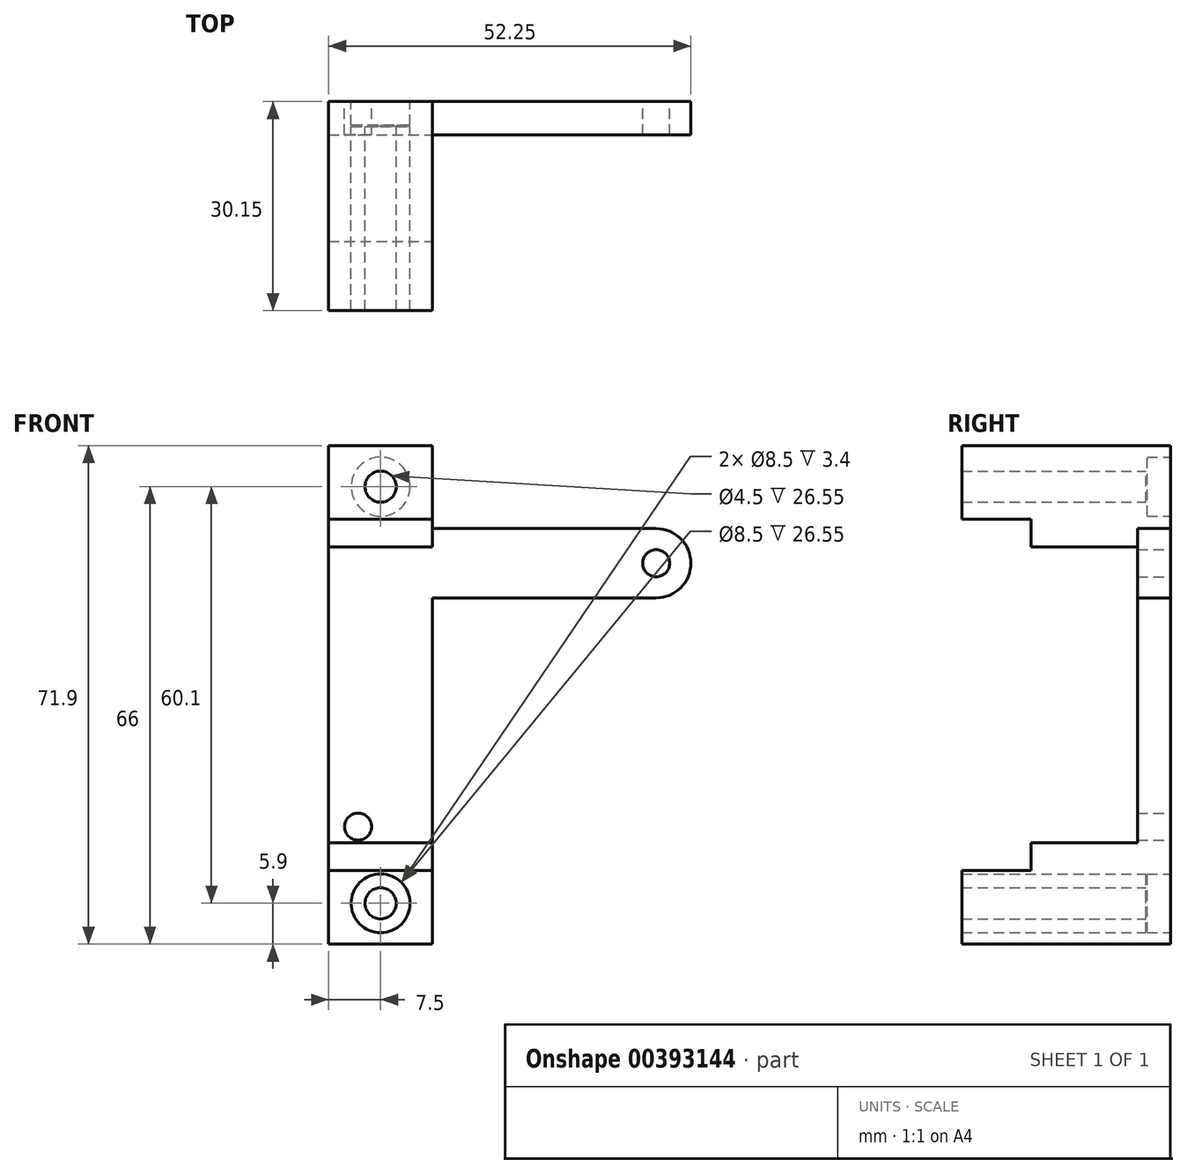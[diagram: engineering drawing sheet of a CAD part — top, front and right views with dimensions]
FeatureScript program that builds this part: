
annotation { "Feature Type Name" : "Feature", "Feature Type Description" : "" }
export const myFeature = defineFeature(function(context is Context, id is Id, definition is map)
    precondition{}
    {
        {
            var Q0;
            Q0=qCreatedBy(makeId("Front.planeOp"),FACE);
            var sketch = newSketch(context, id + "F0", { "sketchPlane" : qUnion([Q0])});
            skLineSegment(sketch, "E0", {"start": v(7.5, 35.95) * mm, "end": v(-7.5, 35.95) * mm});
            skPoint(sketch, "E1", {"position": v(0, 35.95) * mm});
            skLineSegment(sketch, "E2.MirrorCS", {"start": v(7.5, -35.95) * mm, "end": v(-7.5, -35.95) * mm});
            skPoint(sketch, "E3.MirrorP", {"position": v(0, -35.95) * mm});
            skLineSegment(sketch, "E4", {"start": v(-7.5, 35.95) * mm, "end": v(-7.5, -35.95) * mm});
            skLineSegment(sketch, "E5", {"start": v(7.5, -35.95) * mm, "end": v(7.5, 35.95) * mm});
            skLineSegment(sketch, "E6", {"start": v(-7.5, 25.35) * mm, "end": v(7.5, 25.35) * mm});
            skLineSegment(sketch, "E7", {"start": v(-7.5, 21.35) * mm, "end": v(7.5, 21.35) * mm});
            skLineSegment(sketch, "E8.MirrorCS", {"start": v(-7.5, -25.35) * mm, "end": v(7.5, -25.35) * mm});
            skLineSegment(sketch, "E9.MirrorCS", {"start": v(-7.5, -21.35) * mm, "end": v(7.5, -21.35) * mm});
            skCircle(sketch, "E10", {"center": v(0, 30.05) * mm, "radius": 2.25 * mm});
            skCircle(sketch, "E11", {"center": v(0, 30.05) * mm, "radius": 4.25 * mm});
            skCircle(sketch, "E12.MirrorC", {"center": v(0, -30.05) * mm, "radius": 2.25 * mm});
            skCircle(sketch, "E13.MirrorC", {"center": v(0, -30.05) * mm, "radius": 4.25 * mm});
            skCircle(sketch, "E14", {"center": v(39.75, 19) * mm, "radius": 1.95 * mm});
            skCircle(sketch, "E15", {"center": v(-3.25, -19) * mm, "radius": 1.95 * mm});
            skArc(sketch, "E16", {"start": v(39.75, 24) * mm, "mid": v(44.75, 19) * mm, "end": v(39.75, 14) * mm});
            skLineSegment(sketch, "E17", {"start": v(39.75, 24) * mm, "end": v(7.5, 24) * mm});
            skLineSegment(sketch, "E18", {"start": v(39.75, 14) * mm, "end": v(7.5, 14) * mm});
            skSolve(sketch);
        }
        {
            var Q0;
            {var subQ0=sQuery(id+"F0.wireOp",EDGE,"E7");Q0=makeQuery(id+"F0.imprint","IMPRINT",FACE,{"disambiguationData":[TD([[makeQuery(id+"F0.imprint","IMPRINT",EDGE,{"derivedFrom":subQ0}),-1.0]])]});}
            var Q1;
            Q1=makeQuery(id+"F0.imprint","IMPRINT",FACE,{"disambiguationData":[TD([[makeQuery(id+"F0.imprint","IMPRINT",EDGE,{"derivedFrom":sQuery(id+"F0.wireOp",EDGE,"E14")}),-1.0]])]});
            extrude(context, id + "F1", {"entities" : qUnion([Q0, Q1]), "depth" : 4.8 * mm});
        }
        {
            var Q0;
            {var subQ0=sQuery(id+"F0.wireOp",EDGE,"E6");Q0=makeQuery(id+"F0.imprint","IMPRINT",FACE,{"disambiguationData":[TD([[makeQuery(id+"F0.imprint","IMPRINT",EDGE,{"derivedFrom":subQ0}),-1.0]])]});}
            var Q1;
            {var subQ0=sQuery(id+"F0.wireOp",EDGE,"E8.MirrorCS");Q1=makeQuery(id+"F0.imprint","IMPRINT",FACE,{"disambiguationData":[TD([[makeQuery(id+"F0.imprint","IMPRINT",EDGE,{"derivedFrom":subQ0}),1.0]])]});}
            extrude(context, id + "F2", {"entities" : qUnion([Q0, Q1]), "operationType" : NewBodyOperationType.ADD, "depth" : (19.15 + 1) * mm});
        }
        {
            var Q0;
            {var subQ1=sQuery(id+"F0.wireOp",EDGE,"E0");Q0=makeQuery(id+"F0.imprint","IMPRINT",FACE,{"disambiguationData":[TD([[makeQuery(id+"F0.imprint","IMPRINT",EDGE,{"derivedFrom":subQ1}),1.0]])]});}
            var Q1;
            Q1=makeQuery(id+"F0.imprint","IMPRINT",FACE,{"disambiguationData":[TD([[makeQuery(id+"F0.imprint","IMPRINT",EDGE,{"derivedFrom":sQuery(id+"F0.wireOp",EDGE,"E10")}),-1.0]])]});
            var Q2;
            {var subQ2=sQuery(id+"F0.wireOp",EDGE,"E2.MirrorCS");Q2=makeQuery(id+"F0.imprint","IMPRINT",FACE,{"disambiguationData":[TD([[makeQuery(id+"F0.imprint","IMPRINT",EDGE,{"derivedFrom":subQ2}),-1.0]])]});}
            var Q3;
            Q3=makeQuery(id+"F0.imprint","IMPRINT",FACE,{"disambiguationData":[TD([[makeQuery(id+"F0.imprint","IMPRINT",EDGE,{"derivedFrom":sQuery(id+"F0.wireOp",EDGE,"E12.MirrorC")}),1.0]])]});
            extrude(context, id + "F3", {"entities" : qUnion([Q0, Q1, Q2, Q3]), "operationType" : NewBodyOperationType.ADD, "depth" : 30.15 * mm});
        }
        {
            var Q0;
            Q0=makeQuery(id+"F0.imprint","IMPRINT",FACE,{"disambiguationData":[TD([[makeQuery(id+"F0.imprint","IMPRINT",EDGE,{"derivedFrom":sQuery(id+"F0.wireOp",EDGE,"E12.MirrorC")}),1.0]])]});
            var Q1;
            Q1=makeQuery(id+"F0.imprint","IMPRINT",FACE,{"disambiguationData":[TD([[makeQuery(id+"F0.imprint","IMPRINT",EDGE,{"derivedFrom":sQuery(id+"F0.wireOp",EDGE,"E10")}),-1.0]])]});
            extrude(context, id + "F4", {"entities" : qUnion([Q0, Q1]), "operationType" : NewBodyOperationType.REMOVE, "depth" : 3.4 * mm});
        }
        {
            var Q0;
            Q0=makeQuery(id+"F0.imprint","IMPRINT",FACE,{"disambiguationData":[TD([[makeQuery(id+"F0.imprint","IMPRINT",EDGE,{"derivedFrom":sQuery(id+"F0.wireOp",EDGE,"E10")}),1.0]])]});
            var Q1;
            Q1=makeQuery(id+"F0.imprint","IMPRINT",FACE,{"disambiguationData":[TD([[makeQuery(id+"F0.imprint","IMPRINT",EDGE,{"derivedFrom":sQuery(id+"F0.wireOp",EDGE,"E12.MirrorC")}),-1.0]])]});
            extrude(context, id + "F5", {"entities" : qUnion([Q0, Q1]), "operationType" : NewBodyOperationType.ADD, "depth" : 3.6 * mm});
        }
        {
            var Q0;
            Q0=makeQuery(id+"F0.imprint","IMPRINT",FACE,{"disambiguationData":[TD([[makeQuery(id+"F0.imprint","IMPRINT",EDGE,{"derivedFrom":sQuery(id+"F0.wireOp",EDGE,"E12.MirrorC")}),-1.0]])]});
            var Q1;
            Q1=makeQuery(id+"F0.imprint","IMPRINT",FACE,{"disambiguationData":[TD([[makeQuery(id+"F0.imprint","IMPRINT",EDGE,{"derivedFrom":sQuery(id+"F0.wireOp",EDGE,"E10")}),1.0]])]});
            extrude(context, id + "F6", {"entities" : qUnion([Q0, Q1]), "operationType" : NewBodyOperationType.REMOVE, "depth" : 3.4 * mm});
        }
    });
